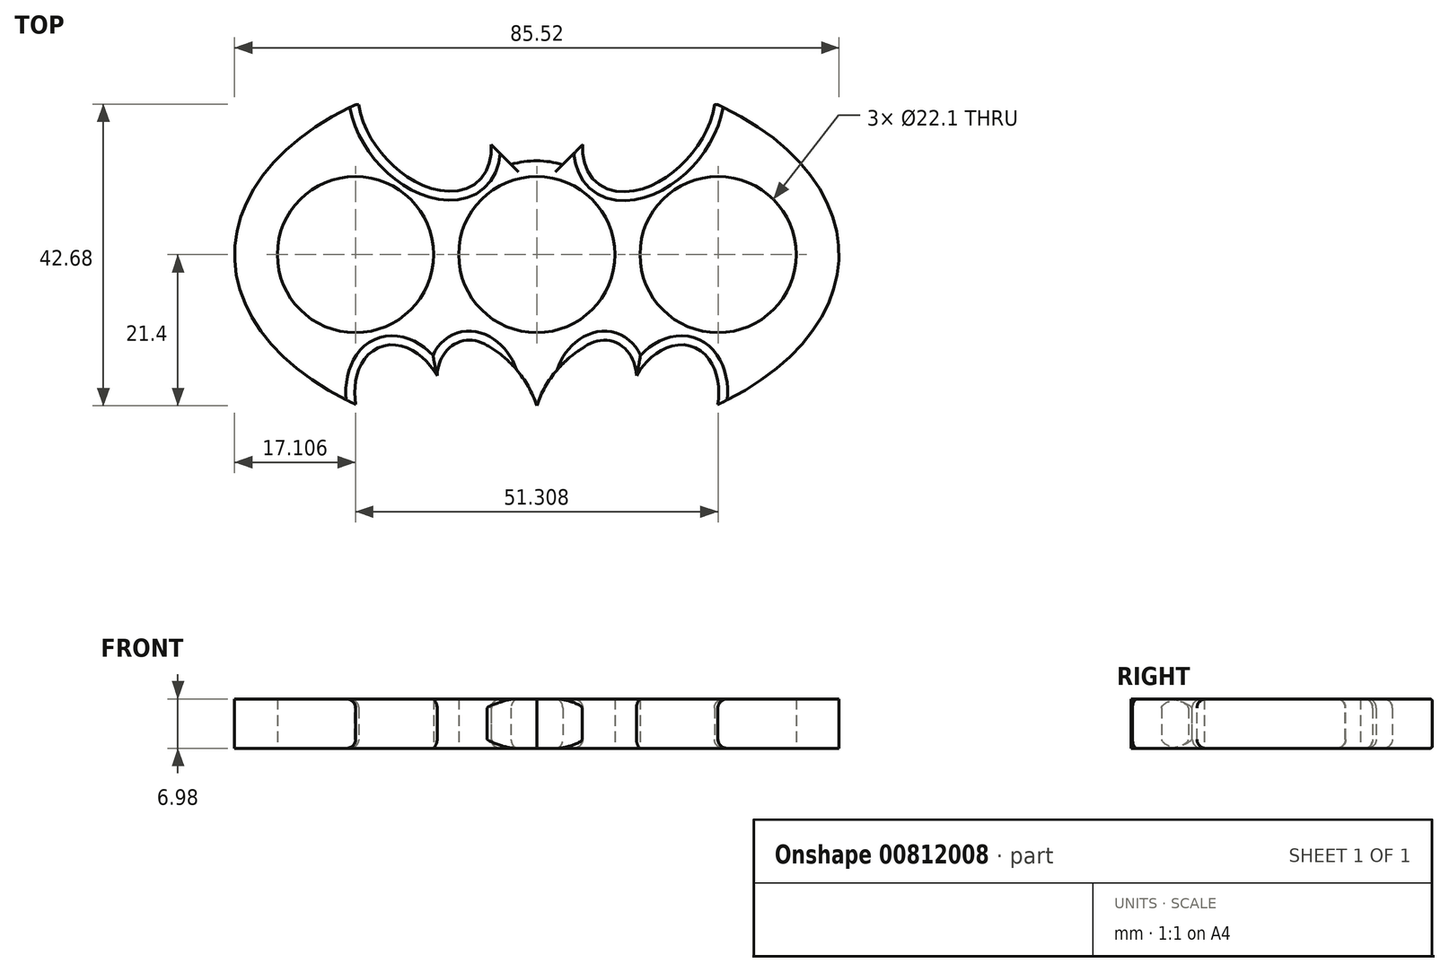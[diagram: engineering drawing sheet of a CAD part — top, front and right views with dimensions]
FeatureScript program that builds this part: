
annotation { "Feature Type Name" : "Feature", "Feature Type Description" : "" }
export const myFeature = defineFeature(function(context is Context, id is Id, definition is map)
    precondition{}
    {
        {
            var Q0;
            Q0=qCreatedBy(makeId("Top.planeOp"),FACE);
            var sketch = newSketch(context, id + "F0", { "sketchPlane" : qUnion([Q0])});
            skCircle(sketch, "E0", {"center": v(0, 0) * mm, "radius": 11.05 * mm});
            skCircle(sketch, "E1", {"center": v(25.65, 0) * mm, "radius": 11.05 * mm});
            skCircle(sketch, "E2", {"center": v(-25.65, 0) * mm, "radius": 11.05 * mm});
            skEllipse(sketch, "E3", {"center": v(0, 0) * mm, "majorRadius": 42.76 * mm, "minorRadius": 26.5 * mm, "majorAxis": v(1, 0)});
            skPoint(sketch, "E4", {"position": v(0, 11.05) * mm});
            skPoint(sketch, "E5", {"position": v(-25.65, 21.2) * mm});
            skLineSegment(sketch, "E6", {"start": v(-25.65, 21.2) * mm, "end": v(25.65, 21.2) * mm});
            skPoint(sketch, "E7", {"position": v(0, 21.2) * mm});
            skPoint(sketch, "E8", {"position": v(-24.47, -10.99) * mm});
            skPoint(sketch, "E9", {"position": v(1.18, -10.99) * mm});
            skPoint(sketch, "E10", {"position": v(26.84, -10.99) * mm});
            skLineSegment(sketch, "E11", {"start": v(-24.47, -10.99) * mm, "end": v(1.18, -10.99) * mm});
            skLineSegment(sketch, "E12", {"start": v(26.84, -10.99) * mm, "end": v(1.18, -10.99) * mm});
            skLineSegment(sketch, "E13", {"start": v(0, 0) * mm, "end": v(-19.73, 23.51) * mm});
            skLineSegment(sketch, "E14", {"start": v(0, 0) * mm, "end": v(19.73, 23.51) * mm});
            skEllipse(sketch, "E15", {"center": v(-15.88, 18.92) * mm, "majorRadius": 11.43 * mm, "minorRadius": 7.62 * mm, "majorAxis": v(0.66, -0.75)});
            skPoint(sketch, "E16", {"position": v(15.87, 18.92) * mm});
            skEllipse(sketch, "E17", {"center": v(15.87, 18.92) * mm, "majorRadius": 11.43 * mm, "minorRadius": 7.62 * mm, "majorAxis": v(-0.64, -0.77)});
            skCircle(sketch, "E18", {"center": v(0, 0) * mm, "radius": 13.26 * mm});
            skLineSegment(sketch, "E19", {"start": v(-6.43, 15.55) * mm, "end": v(6.5, 15.55) * mm});
            skLineSegment(sketch, "E20", {"start": v(-6.43, 15.55) * mm, "end": v(-3.63, 12.76) * mm});
            skLineSegment(sketch, "E21", {"start": v(6.5, 15.55) * mm, "end": v(3.69, 12.74) * mm});
            skLineSegment(sketch, "E22", {"start": v(-25.24, 21.4) * mm, "end": v(0, 21.4) * mm});
            skLineSegment(sketch, "E23", {"start": v(0, 26.5) * mm, "end": v(-1.53, 26.5) * mm});
            skPoint(sketch, "E24", {"position": v(0, -21.4) * mm});
            skLineSegment(sketch, "E25", {"start": v(0, -26.5) * mm, "end": v(1.19, -26.5) * mm});
            skLineSegment(sketch, "E26", {"start": v(0, -21.4) * mm, "end": v(-25.24, -21.4) * mm});
            skLineSegment(sketch, "E27", {"start": v(-25.24, -21.4) * mm, "end": v(0, -21.4) * mm});
            skLineSegment(sketch, "E28", {"start": v(25.24, -21.4) * mm, "end": v(0, -21.4) * mm});
            skEllipse(sketch, "E29", {"center": v(-19.05, -21.4) * mm, "majorRadius": 8.9 * mm, "minorRadius": 6.35 * mm, "majorAxis": v(0.34, -0.94)});
            skEllipse(sketch, "E30", {"center": v(-8.9, -18.35) * mm, "majorRadius": 6.35 * mm, "minorRadius": 5.08 * mm, "majorAxis": v(0.3, -0.95)});
            skArc(sketch, "E31", {"start": v(0, -21.4) * mm, "mid": v(-2.93, -16.21) * mm, "end": v(-7.62, -12.55) * mm});
            skEllipse(sketch, "E32", {"center": v(8.89, -18.35) * mm, "majorRadius": 6.35 * mm, "minorRadius": 5.08 * mm, "majorAxis": v(0.3, 0.95)});
            skEllipse(sketch, "E33", {"center": v(19.05, -21.4) * mm, "majorRadius": 8.9 * mm, "minorRadius": 6.35 * mm, "majorAxis": v(0.34, 0.94)});
            skArc(sketch, "E34", {"start": v(6.41, -13.3) * mm, "mid": v(2.5, -16.78) * mm, "end": v(0, -21.4) * mm});
            skLineSegment(sketch, "E35", {"start": v(19.05, -21.4) * mm, "end": v(22.1, -13.04) * mm});
            skLineSegment(sketch, "E36", {"start": v(-8.9, -18.35) * mm, "end": v(8.9, -18.35) * mm});
            skLineSegment(sketch, "E37", {"start": v(-8.9, -18.35) * mm, "end": v(-10.85, -12.3) * mm});
            skLineSegment(sketch, "E38", {"start": v(8.9, -18.35) * mm, "end": v(10.85, -12.3) * mm});
            skLineSegment(sketch, "E39", {"start": v(-19.05, -21.4) * mm, "end": v(-22.1, -13.04) * mm});
            skSolve(sketch);
        }
        {
            var Q0;
            Q0=makeQuery(id+"F0.imprint","IMPRINT",FACE,{"disambiguationData":[TD([[makeQuery(id+"F0.imprint","IMPRINT",EDGE,{"derivedFrom":sQuery(id+"F0.wireOp",EDGE,"E2")}),-1.0]])]});
            var Q1;
            {var subQ5=sQuery(id+"F0.wireOp",EDGE,"E20");Q1=makeQuery(id+"F0.imprint","IMPRINT",FACE,{"disambiguationData":[TD([[makeQuery(id+"F0.imprint","IMPRINT",EDGE,{"derivedFrom":subQ5}),-1.0]])]});}
            var Q2;
            {var subQ4=sQuery(id+"F0.wireOp",EDGE,"E0");var subQ6=sQuery(id+"F0.wireOp",EDGE,"E13");var subQ7=makeQuery(id+"F0.imprint","INTERSECT",VERTEX,{"derivedFrom":[subQ4,subQ6]});Q2=makeQuery(id+"F0.imprint","IMPRINT",FACE,{"disambiguationData":[TD([[makeQuery(id+"F0.imprint","IMPRINT",EDGE,{"disambiguationData":[TD([[subQ7,1.0]])],"derivedFrom":subQ4}),-1.0]])]});}
            var Q3;
            {var subQ0=sQuery(id+"F0.wireOp",EDGE,"E11");var subQ1=sQuery(id+"F0.wireOp",EDGE,"E0");var subQ2=makeQuery(id+"F0.imprint","INTERSECT",VERTEX,{"derivedFrom":[subQ1,subQ0]});Q3=makeQuery(id+"F0.imprint","IMPRINT",FACE,{"disambiguationData":[TD([[makeQuery(id+"F0.imprint","IMPRINT",EDGE,{"disambiguationData":[TD([[subQ2,1.0]])],"derivedFrom":subQ1}),-1.0]])]});}
            var Q4;
            {var subQ5=sQuery(id+"F0.wireOp",EDGE,"E21");Q4=makeQuery(id+"F0.imprint","IMPRINT",FACE,{"disambiguationData":[TD([[makeQuery(id+"F0.imprint","IMPRINT",EDGE,{"derivedFrom":subQ5}),1.0]])]});}
            var Q5;
            {var subQ0=sQuery(id+"F0.wireOp",EDGE,"E12");var subQ1=sQuery(id+"F0.wireOp",EDGE,"E0");var subQ2=makeQuery(id+"F0.imprint","INTERSECT",VERTEX,{"derivedFrom":[subQ1,subQ0]});Q5=makeQuery(id+"F0.imprint","IMPRINT",FACE,{"disambiguationData":[TD([[makeQuery(id+"F0.imprint","IMPRINT",EDGE,{"disambiguationData":[TD([[subQ2,-1.0]])],"derivedFrom":subQ1}),-1.0]])]});}
            var Q6;
            {var subQ0=sQuery(id+"F0.wireOp",EDGE,"E11");var subQ1=sQuery(id+"F0.wireOp",EDGE,"E0");var subQ2=makeQuery(id+"F0.imprint","INTERSECT",VERTEX,{"derivedFrom":[subQ1,subQ0]});Q6=makeQuery(id+"F0.imprint","IMPRINT",FACE,{"disambiguationData":[TD([[makeQuery(id+"F0.imprint","IMPRINT",EDGE,{"disambiguationData":[TD([[subQ2,-1.0]])],"derivedFrom":subQ1}),-1.0]])]});}
            var Q7;
            {var subQ1=sQuery(id+"F0.wireOp",EDGE,"E31");var subQ3=sQuery(id+"F0.wireOp",EDGE,"E36");var subQ4=makeQuery(id+"F0.imprint","INTERSECT",VERTEX,{"derivedFrom":[subQ1,subQ3]});Q7=makeQuery(id+"F0.imprint","IMPRINT",FACE,{"disambiguationData":[TD([[makeQuery(id+"F0.imprint","IMPRINT",EDGE,{"disambiguationData":[TD([[subQ4,-1.0]])],"derivedFrom":subQ3}),-1.0]])]});}
            extrude(context, id + "F1", {"entities" : qUnion([Q0, Q1, Q2, Q3, Q4, Q5, Q6, Q7]), "endBound" : BoundingType.SYMMETRIC, "depth" : 7 * mm, "offsetDistance" : 25.4 * mm});
        }
        {
            var Q0;
            Q0=makeQuery(id+"F1.opExtrude","CAP_EDGE",EDGE,{"disambiguationData":[OSD([sQuery(id+"F0.wireOp",EDGE,"E15")])],"isStart":false});
            var Q1;
            Q1=makeQuery(id+"F1.opExtrude","CAP_EDGE",EDGE,{"disambiguationData":[OSD([sQuery(id+"F0.wireOp",EDGE,"E17")])],"isStart":false});
            var Q2;
            Q2=makeQuery(id+"F1.opExtrude","CAP_EDGE",EDGE,{"disambiguationData":[OSD([sQuery(id+"F0.wireOp",EDGE,"E18")])],"isStart":false});
            var Q3;
            Q3=makeQuery(id+"F1.opExtrude","CAP_EDGE",EDGE,{"disambiguationData":[OSD([sQuery(id+"F0.wireOp",EDGE,"E32")])],"isStart":false});
            var Q4;
            Q4=makeQuery(id+"F1.opExtrude","CAP_EDGE",EDGE,{"disambiguationData":[OSD([sQuery(id+"F0.wireOp",EDGE,"E33")])],"isStart":false});
            var Q5;
            Q5=makeQuery(id+"F1.opExtrude","CAP_EDGE",EDGE,{"disambiguationData":[OSD([sQuery(id+"F0.wireOp",EDGE,"E30")])],"isStart":false});
            var Q6;
            Q6=makeQuery(id+"F1.opExtrude","CAP_EDGE",EDGE,{"disambiguationData":[OSD([sQuery(id+"F0.wireOp",EDGE,"E29")])],"isStart":false});
            var Q7;
            Q7=makeQuery(id+"F1.opExtrude","CAP_EDGE",EDGE,{"disambiguationData":[OSD([sQuery(id+"F0.wireOp",EDGE,"E18")])],"isStart":true});
            var Q8;
            Q8=makeQuery(id+"F1.opExtrude","CAP_EDGE",EDGE,{"disambiguationData":[OSD([sQuery(id+"F0.wireOp",EDGE,"E17")])],"isStart":true});
            var Q9;
            Q9=makeQuery(id+"F1.opExtrude","CAP_EDGE",EDGE,{"disambiguationData":[OSD([sQuery(id+"F0.wireOp",EDGE,"E15")])],"isStart":true});
            var Q10;
            Q10=makeQuery(id+"F1.opExtrude","CAP_EDGE",EDGE,{"disambiguationData":[OSD([sQuery(id+"F0.wireOp",EDGE,"E33")])],"isStart":true});
            var Q11;
            Q11=makeQuery(id+"F1.opExtrude","CAP_EDGE",EDGE,{"disambiguationData":[OSD([sQuery(id+"F0.wireOp",EDGE,"E32")])],"isStart":true});
            var Q12;
            Q12=makeQuery(id+"F1.opExtrude","CAP_EDGE",EDGE,{"disambiguationData":[OSD([sQuery(id+"F0.wireOp",EDGE,"E30")])],"isStart":true});
            var Q13;
            Q13=makeQuery(id+"F1.opExtrude","CAP_EDGE",EDGE,{"disambiguationData":[OSD([sQuery(id+"F0.wireOp",EDGE,"E29")])],"isStart":true});
            fillet(context, id + "F2", {"entities" : qUnion([Q0, Q1, Q2, Q3, Q4, Q5, Q6, Q7, Q8, Q9, Q10, Q11, Q12, Q13]), "radius" : 1.27 * mm, "tangentPropagation" : true, "allowEdgeOverflow" : false});
        }
        {
            var Q0;
            Q0=qCreatedBy(makeId("Top.planeOp"),FACE);
            var sketch = newSketch(context, id + "F3", { "sketchPlane" : qUnion([Q0])});
            skCircle(sketch, "E40", {"center": v(0, 0) * mm, "radius": 11.01 * mm});
            skSolve(sketch);
        }
        {
            var Q0;
            Q0 = qSketchRegion(id + "F3", true);
            extrude(context, id + "F4", {"entities" : qUnion([Q0]), "operationType" : NewBodyOperationType.REMOVE, "oppositeDirection" : true, "depth" : 25.4 * mm, "offsetDistance" : 25.4 * mm});
        }
    });
